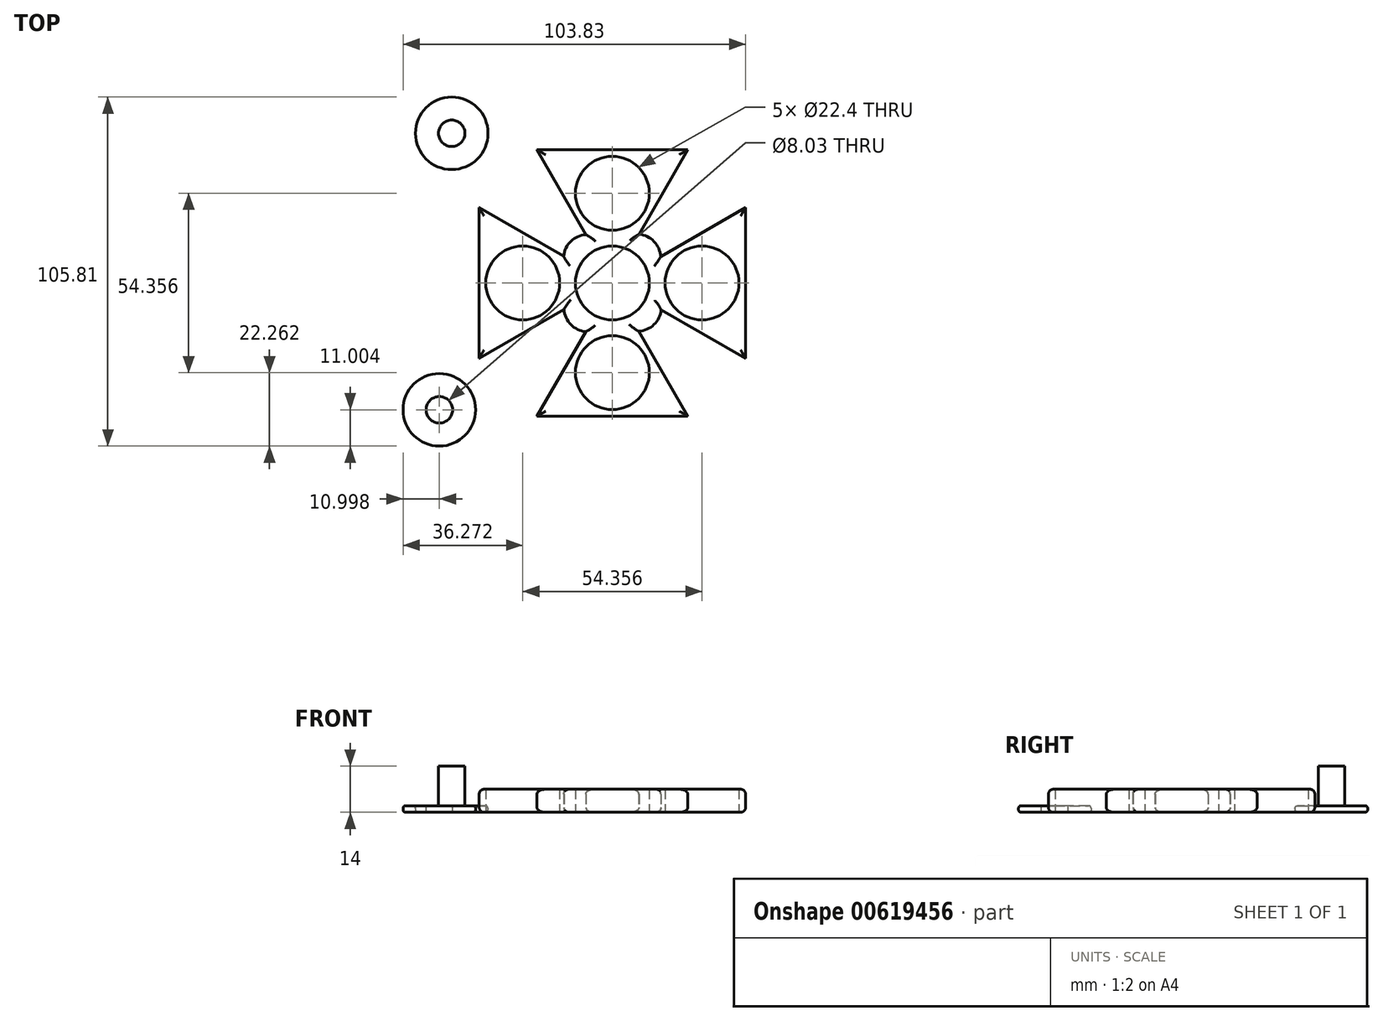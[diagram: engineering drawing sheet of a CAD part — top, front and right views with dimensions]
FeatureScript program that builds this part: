
annotation { "Feature Type Name" : "Feature", "Feature Type Description" : "" }
export const myFeature = defineFeature(function(context is Context, id is Id, definition is map)
    precondition{}
    {
        {
            var Q0;
            Q0=qCreatedBy(makeId("Top.planeOp"),FACE);
            var sketch = newSketch(context, id + "F0", { "sketchPlane" : qUnion([Q0])});
            skCircle(sketch, "E0", {"center": v(0, 0) * mm, "radius": 11.2 * mm});
            skArc(sketch, "E1", {"start": v(-11.62, -6.26) * mm, "mid": v(-11.52, -6.45) * mm, "end": v(-11.41, -6.63) * mm});
            skCircle(sketch, "E2", {"center": v(0, 27.18) * mm, "radius": 11.2 * mm});
            skCircle(sketch, "E3.1.1", {"center": v(-27.18, 0) * mm, "radius": 11.2 * mm});
            skCircle(sketch, "E3.2.1", {"center": v(0, -27.18) * mm, "radius": 11.2 * mm});
            skPoint(sketch, "E4.end.orphan", {"position": v(-13.2, 0) * mm});
            skCircle(sketch, "E5.2.3.0", {"center": v(27.18, 0) * mm, "radius": 11.2 * mm});
            skLineSegment(sketch, "E6.0", {"start": v(-40.38, -22.86) * mm, "end": v(-40.38, 22.86) * mm});
            skLineSegment(sketch, "E6.1", {"start": v(-40.38, 22.86) * mm, "end": v(-14.76, 8.07) * mm});
            skLineSegment(sketch, "E6.2", {"start": v(-14.65, -8) * mm, "end": v(-40.38, -22.86) * mm});
            skPoint(sketch, "E6.0.midPoint", {"position": v(-40.38, 0) * mm});
            skLineSegment(sketch, "E7.1.0", {"start": v(-22.86, -40.38) * mm, "end": v(-8.07, -14.76) * mm});
            skLineSegment(sketch, "E7.1.1", {"start": v(22.86, -40.38) * mm, "end": v(-22.86, -40.38) * mm});
            skLineSegment(sketch, "E7.1.2", {"start": v(8, -14.65) * mm, "end": v(22.86, -40.38) * mm});
            skLineSegment(sketch, "E7.2.0", {"start": v(40.38, -22.86) * mm, "end": v(14.76, -8.07) * mm});
            skLineSegment(sketch, "E7.2.1", {"start": v(40.38, 22.86) * mm, "end": v(40.38, -22.86) * mm});
            skLineSegment(sketch, "E7.2.2", {"start": v(14.65, 8) * mm, "end": v(40.38, 22.86) * mm});
            skLineSegment(sketch, "E7.3.0", {"start": v(22.86, 40.38) * mm, "end": v(8.07, 14.76) * mm});
            skLineSegment(sketch, "E7.3.1", {"start": v(-22.86, 40.38) * mm, "end": v(22.86, 40.38) * mm});
            skLineSegment(sketch, "E7.3.2", {"start": v(-8, 14.65) * mm, "end": v(-22.86, 40.38) * mm});
            skArc(sketch, "E8", {"start": v(-8, 14.65) * mm, "mid": v(-12.6, 12.6) * mm, "end": v(-14.76, 8.07) * mm});
            skArc(sketch, "E9.1.0", {"start": v(-14.65, -8) * mm, "mid": v(-12.6, -12.6) * mm, "end": v(-8.07, -14.76) * mm});
            skArc(sketch, "E9.2.0", {"start": v(8, -14.65) * mm, "mid": v(12.6, -12.6) * mm, "end": v(14.76, -8.07) * mm});
            skArc(sketch, "E9.3.0", {"start": v(14.65, 8) * mm, "mid": v(12.6, 12.6) * mm, "end": v(8.07, 14.76) * mm});
            skPoint(sketch, "E10.orphan", {"position": v(0, 0.78) * mm});
            skPoint(sketch, "E11.orphan", {"position": v(0.78, 0) * mm});
            skPoint(sketch, "E12.orphan", {"position": v(0, -0.78) * mm});
            skPoint(sketch, "E13.orphan", {"position": v(-0.78, 0) * mm});
            skSolve(sketch);
        }
        {
            var Q0;
            Q0=makeQuery(id+"F0.imprint","IMPRINT",FACE,{"disambiguationData":[TD([[makeQuery(id+"F0.imprint","IMPRINT",EDGE,{"derivedFrom":sQuery(id+"F0.wireOp",EDGE,"E0")}),-1.0]])]});
            extrude(context, id + "F1", {"entities" : qUnion([Q0]), "depth" : 7 * mm, "offsetDistance" : 25 * mm});
        }
        {
            var Q0;
            Q0=makeQuery(id+"F1.opExtrude","CAP_EDGE",EDGE,{"disambiguationData":[OSD([sQuery(id+"F0.wireOp",EDGE,"E7.1.1")])],"isStart":false});
            var Q1;
            Q1=makeQuery(id+"F1.opExtrude","CAP_EDGE",EDGE,{"disambiguationData":[OSD([sQuery(id+"F0.wireOp",EDGE,"E7.1.0")])],"isStart":false});
            var Q2;
            Q2=makeQuery(id+"F1.opExtrude","CAP_EDGE",EDGE,{"disambiguationData":[OSD([sQuery(id+"F0.wireOp",EDGE,"E9.1.0")])],"isStart":false});
            var Q3;
            Q3=makeQuery(id+"F1.opExtrude","CAP_EDGE",EDGE,{"disambiguationData":[OSD([sQuery(id+"F0.wireOp",EDGE,"E6.2")])],"isStart":false});
            var Q4;
            Q4=makeQuery(id+"F1.opExtrude","CAP_EDGE",EDGE,{"disambiguationData":[OSD([sQuery(id+"F0.wireOp",EDGE,"E6.0")])],"isStart":false});
            var Q5;
            Q5=makeQuery(id+"F1.opExtrude","CAP_EDGE",EDGE,{"disambiguationData":[OSD([sQuery(id+"F0.wireOp",EDGE,"E6.1")])],"isStart":false});
            var Q6;
            Q6=makeQuery(id+"F1.opExtrude","CAP_EDGE",EDGE,{"disambiguationData":[OSD([sQuery(id+"F0.wireOp",EDGE,"E8")])],"isStart":false});
            var Q7;
            Q7=makeQuery(id+"F1.opExtrude","CAP_EDGE",EDGE,{"disambiguationData":[OSD([sQuery(id+"F0.wireOp",EDGE,"E7.3.2")])],"isStart":false});
            var Q8;
            Q8=makeQuery(id+"F1.opExtrude","CAP_EDGE",EDGE,{"disambiguationData":[OSD([sQuery(id+"F0.wireOp",EDGE,"E7.3.1")])],"isStart":false});
            var Q9;
            Q9=makeQuery(id+"F1.opExtrude","CAP_EDGE",EDGE,{"disambiguationData":[OSD([sQuery(id+"F0.wireOp",EDGE,"E7.3.0")])],"isStart":false});
            var Q10;
            Q10=makeQuery(id+"F1.opExtrude","CAP_EDGE",EDGE,{"disambiguationData":[OSD([sQuery(id+"F0.wireOp",EDGE,"E7.2.2")])],"isStart":false});
            var Q11;
            Q11=makeQuery(id+"F1.opExtrude","CAP_EDGE",EDGE,{"disambiguationData":[OSD([sQuery(id+"F0.wireOp",EDGE,"E9.3.0")])],"isStart":false});
            var Q12;
            Q12=makeQuery(id+"F1.opExtrude","CAP_EDGE",EDGE,{"disambiguationData":[OSD([sQuery(id+"F0.wireOp",EDGE,"E7.2.1")])],"isStart":false});
            var Q13;
            Q13=makeQuery(id+"F1.opExtrude","CAP_EDGE",EDGE,{"disambiguationData":[OSD([sQuery(id+"F0.wireOp",EDGE,"E7.2.0")])],"isStart":false});
            var Q14;
            Q14=makeQuery(id+"F1.opExtrude","CAP_EDGE",EDGE,{"disambiguationData":[OSD([sQuery(id+"F0.wireOp",EDGE,"E9.2.0")])],"isStart":false});
            var Q15;
            Q15=makeQuery(id+"F1.opExtrude","CAP_EDGE",EDGE,{"disambiguationData":[OSD([sQuery(id+"F0.wireOp",EDGE,"E7.1.2")])],"isStart":false});
            fillet(context, id + "F2", {"entities" : qUnion([Q0, Q1, Q2, Q3, Q4, Q5, Q6, Q7, Q8, Q9, Q10, Q11, Q12, Q13, Q14, Q15]), "radius" : 1.5 * mm, "tangentPropagation" : true, "allowEdgeOverflow" : false});
        }
        {
            var Q0;
            Q0=makeQuery(id+"F1.opExtrude","CAP_EDGE",EDGE,{"disambiguationData":[OSD([sQuery(id+"F0.wireOp",EDGE,"E7.1.1")])],"isStart":true});
            var Q1;
            Q1=makeQuery(id+"F1.opExtrude","CAP_EDGE",EDGE,{"disambiguationData":[OSD([sQuery(id+"F0.wireOp",EDGE,"E7.1.2")])],"isStart":true});
            var Q2;
            Q2=makeQuery(id+"F1.opExtrude","CAP_EDGE",EDGE,{"disambiguationData":[OSD([sQuery(id+"F0.wireOp",EDGE,"E7.1.0")])],"isStart":true});
            var Q3;
            Q3=makeQuery(id+"F1.opExtrude","CAP_EDGE",EDGE,{"disambiguationData":[OSD([sQuery(id+"F0.wireOp",EDGE,"E6.0")])],"isStart":true});
            var Q4;
            Q4=makeQuery(id+"F1.opExtrude","CAP_EDGE",EDGE,{"disambiguationData":[OSD([sQuery(id+"F0.wireOp",EDGE,"E6.2")])],"isStart":true});
            var Q5;
            Q5=makeQuery(id+"F1.opExtrude","CAP_EDGE",EDGE,{"disambiguationData":[OSD([sQuery(id+"F0.wireOp",EDGE,"E6.1")])],"isStart":true});
            var Q6;
            Q6=makeQuery(id+"F1.opExtrude","CAP_EDGE",EDGE,{"disambiguationData":[OSD([sQuery(id+"F0.wireOp",EDGE,"E9.1.0")])],"isStart":true});
            var Q7;
            Q7=makeQuery(id+"F1.opExtrude","CAP_EDGE",EDGE,{"disambiguationData":[OSD([sQuery(id+"F0.wireOp",EDGE,"E8")])],"isStart":true});
            var Q8;
            Q8=makeQuery(id+"F1.opExtrude","CAP_EDGE",EDGE,{"disambiguationData":[OSD([sQuery(id+"F0.wireOp",EDGE,"E7.3.2")])],"isStart":true});
            var Q9;
            Q9=makeQuery(id+"F1.opExtrude","CAP_EDGE",EDGE,{"disambiguationData":[OSD([sQuery(id+"F0.wireOp",EDGE,"E7.3.1")])],"isStart":true});
            var Q10;
            Q10=makeQuery(id+"F1.opExtrude","CAP_EDGE",EDGE,{"disambiguationData":[OSD([sQuery(id+"F0.wireOp",EDGE,"E7.3.0")])],"isStart":true});
            var Q11;
            Q11=makeQuery(id+"F1.opExtrude","CAP_EDGE",EDGE,{"disambiguationData":[OSD([sQuery(id+"F0.wireOp",EDGE,"E9.3.0")])],"isStart":true});
            var Q12;
            Q12=makeQuery(id+"F1.opExtrude","CAP_EDGE",EDGE,{"disambiguationData":[OSD([sQuery(id+"F0.wireOp",EDGE,"E7.2.2")])],"isStart":true});
            var Q13;
            Q13=makeQuery(id+"F1.opExtrude","CAP_EDGE",EDGE,{"disambiguationData":[OSD([sQuery(id+"F0.wireOp",EDGE,"E7.2.1")])],"isStart":true});
            var Q14;
            Q14=makeQuery(id+"F1.opExtrude","CAP_EDGE",EDGE,{"disambiguationData":[OSD([sQuery(id+"F0.wireOp",EDGE,"E7.2.0")])],"isStart":true});
            var Q15;
            Q15=makeQuery(id+"F1.opExtrude","CAP_EDGE",EDGE,{"disambiguationData":[OSD([sQuery(id+"F0.wireOp",EDGE,"E9.2.0")])],"isStart":true});
            fillet(context, id + "F3", {"entities" : qUnion([Q0, Q1, Q2, Q3, Q4, Q5, Q6, Q7, Q8, Q9, Q10, Q11, Q12, Q13, Q14, Q15]), "radius" : 1.5 * mm, "tangentPropagation" : true, "allowEdgeOverflow" : false});
        }
        {
            var Q0;
            Q0=qCreatedBy(makeId("Top.planeOp"),FACE);
            var sketch = newSketch(context, id + "F4", { "sketchPlane" : qUnion([Q0])});
            skCircle(sketch, "E14", {"center": v(-48.7, 45.37) * mm, "radius": 11 * mm});
            skSolve(sketch);
        }
        {
            var Q0;
            Q0=makeQuery(id+"F4.imprint","IMPRINT",FACE,{"disambiguationData":[TD([[makeQuery(id+"F4.imprint","IMPRINT",EDGE,{"derivedFrom":sQuery(id+"F4.wireOp",EDGE,"E14")}),1.0]])]});
            extrude(context, id + "F5", {"entities" : qUnion([Q0]), "depth" : 2 * mm, "offsetDistance" : 25 * mm});
        }
        {
            var Q0;
            Q0=makeQuery(id+"F5.opExtrude","CAP_FACE",FACE,{"disambiguationData":[OSD([sQuery(id+"F4.wireOp",EDGE,"E14")])],"isStart":false});
            var sketch = newSketch(context, id + "F6", { "sketchPlane" : qUnion([Q0])});
            skCircle(sketch, "E15", {"center": v(-48.7, 45.37) * mm, "radius": 4 * mm});
            skSolve(sketch);
        }
        {
            var Q0;
            Q0=makeQuery(id+"F6.imprint","IMPRINT",FACE,{"disambiguationData":[TD([[makeQuery(id+"F6.imprint","IMPRINT",EDGE,{"derivedFrom":sQuery(id+"F6.wireOp",EDGE,"E15")}),1.0]])]});
            extrude(context, id + "F7", {"entities" : qUnion([Q0]), "operationType" : NewBodyOperationType.ADD, "depth" : 12 * mm, "offsetDistance" : 25 * mm});
        }
        {
            var Q0;
            Q0=makeQuery(id+"F5.opExtrude","CAP_EDGE",EDGE,{"disambiguationData":[OSD([sQuery(id+"F4.wireOp",EDGE,"E14")])],"isStart":false});
            var Q1;
            Q1=makeQuery(id+"F5.opExtrude","CAP_EDGE",EDGE,{"disambiguationData":[OSD([sQuery(id+"F4.wireOp",EDGE,"E14")])],"isStart":true});
            fillet(context, id + "F8", {"entities" : qUnion([Q0, Q1]), "radius" : 0.76 * mm, "tangentPropagation" : true, "allowEdgeOverflow" : false});
        }
        {
            var Q0;
            Q0=qCreatedBy(makeId("Top.planeOp"),FACE);
            var sketch = newSketch(context, id + "F9", { "sketchPlane" : qUnion([Q0])});
            skCircle(sketch, "E16", {"center": v(-52.45, -38.44) * mm, "radius": 11 * mm});
            skSolve(sketch);
        }
        {
            var Q0;
            Q0=makeQuery(id+"F9.imprint","IMPRINT",FACE,{"disambiguationData":[TD([[makeQuery(id+"F9.imprint","IMPRINT",EDGE,{"derivedFrom":sQuery(id+"F9.wireOp",EDGE,"E16")}),1.0]])]});
            extrude(context, id + "F10", {"entities" : qUnion([Q0]), "depth" : 2 * mm, "offsetDistance" : 25 * mm});
        }
        {
            var Q0;
            Q0=makeQuery(id+"F10.opExtrude","CAP_FACE",FACE,{"disambiguationData":[OSD([sQuery(id+"F9.wireOp",EDGE,"E16")])],"isStart":false});
            var sketch = newSketch(context, id + "F11", { "sketchPlane" : qUnion([Q0])});
            skCircle(sketch, "E17", {"center": v(-52.45, -38.44) * mm, "radius": 4.01 * mm});
            skSolve(sketch);
        }
        {
            var Q0;
            Q0=makeQuery(id+"F11.imprint","IMPRINT",FACE,{"disambiguationData":[TD([[makeQuery(id+"F11.imprint","IMPRINT",EDGE,{"derivedFrom":sQuery(id+"F11.wireOp",EDGE,"E17")}),1.0]])]});
            extrude(context, id + "F12", {"entities" : qUnion([Q0]), "operationType" : NewBodyOperationType.REMOVE, "depth" : 2 * mm, "offsetDistance" : 25 * mm});
        }
        {
            var Q0;
            Q0=makeQuery(id+"F10.opExtrude","CAP_FACE",FACE,{"disambiguationData":[OSD([sQuery(id+"F9.wireOp",EDGE,"E16")])],"isStart":false});
            var sketch = newSketch(context, id + "F13", { "sketchPlane" : qUnion([Q0])});
            skCircle(sketch, "E18", {"center": v(-52.45, -38.44) * mm, "radius": 4.01 * mm});
            skSolve(sketch);
        }
        {
            var Q0;
            Q0=makeQuery(id+"F13.imprint","IMPRINT",FACE,{"disambiguationData":[TD([[makeQuery(id+"F13.imprint","IMPRINT",EDGE,{"derivedFrom":sQuery(id+"F13.wireOp",EDGE,"E18")}),1.0]])]});
            extrude(context, id + "F14", {"entities" : qUnion([Q0]), "operationType" : NewBodyOperationType.REMOVE, "oppositeDirection" : true, "depth" : 2 * mm, "offsetDistance" : 25 * mm});
        }
        {
            var Q0;
            Q0=makeQuery(id+"F10.opExtrude","CAP_EDGE",EDGE,{"disambiguationData":[OSD([sQuery(id+"F9.wireOp",EDGE,"E16")])],"isStart":false});
            var Q1;
            Q1=makeQuery(id+"F10.opExtrude","CAP_EDGE",EDGE,{"disambiguationData":[OSD([sQuery(id+"F9.wireOp",EDGE,"E16")])],"isStart":true});
            fillet(context, id + "F15", {"entities" : qUnion([Q0, Q1]), "radius" : 0.76 * mm, "tangentPropagation" : true, "allowEdgeOverflow" : false});
        }
    });
